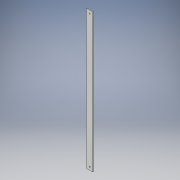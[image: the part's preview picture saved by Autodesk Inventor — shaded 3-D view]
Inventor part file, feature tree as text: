
AUTODESK INVENTOR PART (.ipt)
format: ipt  version: 2018 (Build 220112000, 112)  size: 100,352 bytes
history: native  units: in
note: dims shown in document units (in); Inventor stores cm internally (conversion verified against a paired STEP export)
features: extrude x1, sketch x1
ambient origin geometry x8: Origin, YZ Plane, XZ Plane, XY Plane, X Axis, Y Axis, Z Axis, Center Point
bodies: Solid1 (feature_tree)
feature tree (2):
  extrude  "Extrusion1"  Depth=0.125in
  sketch  "Sketch1"  dims[d0=1.0in d2=0.5in d3=0.2031in d4=0.5in d5=0.125in d6=0.0in d7=22.091in]
